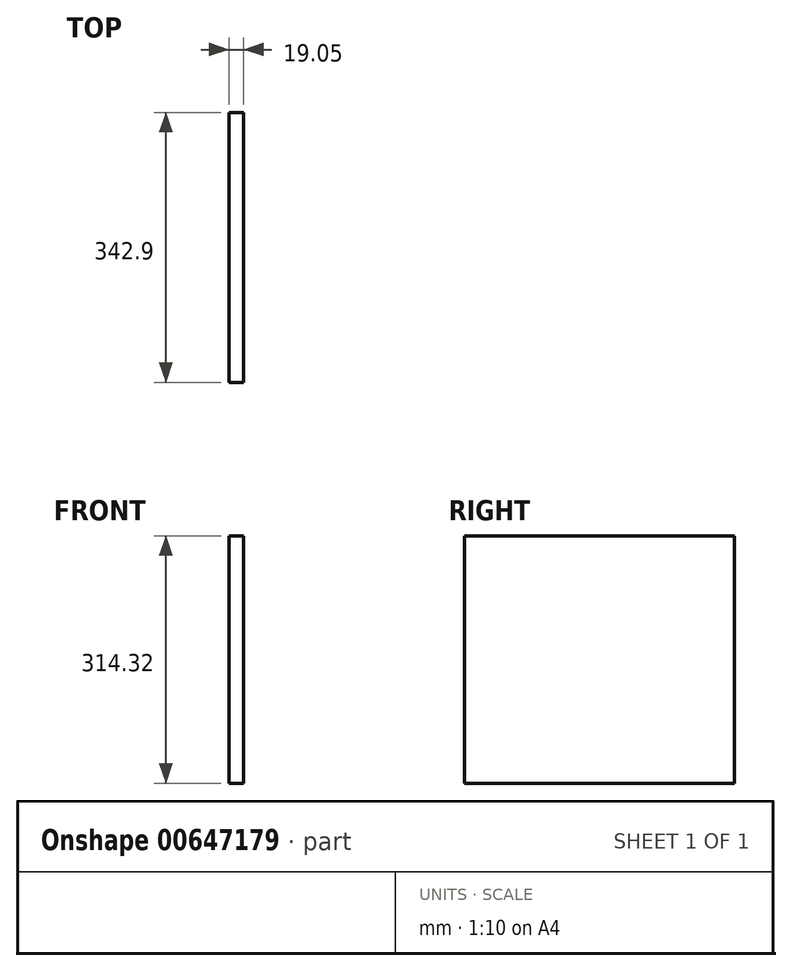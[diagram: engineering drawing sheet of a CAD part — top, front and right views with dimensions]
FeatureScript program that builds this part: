
annotation { "Feature Type Name" : "Feature", "Feature Type Description" : "" }
export const myFeature = defineFeature(function(context is Context, id is Id, definition is map)
    precondition{}
    {
        {
            var Q0;
            Q0=qCreatedBy(makeId("Right.planeOp"),FACE);
            var sketch = newSketch(context, id + "F0", { "sketchPlane" : qUnion([Q0])});
            skLineSegment(sketch, "E0.bottom", {"start": v(171.45, 157.16) * mm, "end": v(-171.45, 157.16) * mm});
            skLineSegment(sketch, "E0.top", {"start": v(171.45, -157.16) * mm, "end": v(-171.45, -157.16) * mm});
            skLineSegment(sketch, "E0.left", {"start": v(171.45, 157.16) * mm, "end": v(171.45, -157.16) * mm});
            skLineSegment(sketch, "E0.right", {"start": v(-171.45, 157.16) * mm, "end": v(-171.45, -157.16) * mm});
            skPoint(sketch, "E0.middle", {"position": v(0, 0) * mm});
            skSolve(sketch);
        }
        {
            var Q0;
            Q0=makeQuery(id+"F0.imprint","IMPRINT",FACE,{"disambiguationData":[TD([[makeQuery(id+"F0.imprint","IMPRINT",EDGE,{"derivedFrom":sQuery(id+"F0.wireOp",EDGE,"E0.bottom")}),1.0]])]});
            extrude(context, id + "F1", {"entities" : qUnion([Q0]), "depth" : 19.05 * mm, "offsetDistance" : 25.4 * mm});
        }
    });
